# Revit family: Recycling-Waste-Bins_Sessanta-Double-Waste-unit_Busch-Systems
name_source: partatom
category: Generic Models
units: mm (PartAtom-declared; Revit-internal decimal feet)

## family parameters
Always vertical = Yes
Can host rebar = No
Cut with Voids When Loaded = No
Maintain Annotation Orientation = No
Part Type = Normal
Room Calculation Point = No
Round Connector Dimension = Use Diameter
Shared = No
Work Plane-Based = No

## types (2) — shared parameters
Body Material = Slate
Container Material = Slate
Default Elevation = 0' - 0"
Dimension (H x W x D) = 54”H x 37”W x 22”D
Keynote = 11 82 00
Manufacturer = Busch Systems International Inc.
Model = Sessanta
Product Page URL = https://www.arcat.com
Top Material = Silver
URL = https://www.buschsystems.com

## per-type parameters (varying)
| type | Product Name | Shelf | Sign Frame |
| SESSANTA - Double - Recyclables - Waste - Full - Slate | SESSANTA - Double - Recyclables - Waste - Full - Slate | No | Yes |
| SESSANTA - Double - Unit - Restaurant - Full - Slate | SESSANTA - Triple - Unit - Restaurant - Full - Slate | Yes | No |

## geometry (parser evidence)
native form markers: Sweep x4
no freeform markers — native parametric forms only
